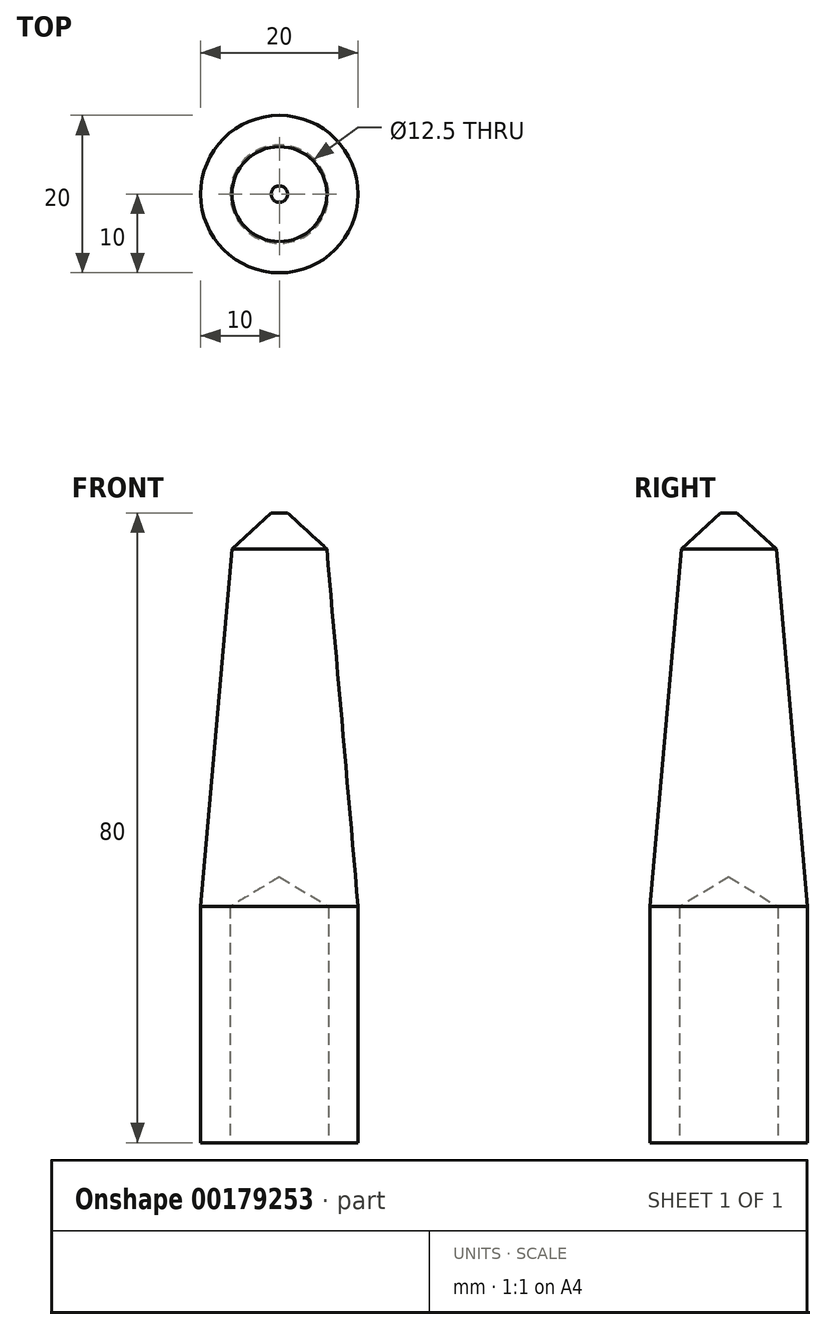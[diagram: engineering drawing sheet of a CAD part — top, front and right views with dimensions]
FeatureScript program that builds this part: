
annotation { "Feature Type Name" : "Feature", "Feature Type Description" : "" }
export const myFeature = defineFeature(function(context is Context, id is Id, definition is map)
    precondition{}
    {
        {
            var Q0;
            Q0=qCreatedBy(makeId("Top.planeOp"),FACE);
            var sketch = newSketch(context, id + "F0", { "sketchPlane" : qUnion([Q0])});
            skPoint(sketch, "E0", {"position": v(0, 0) * mm});
            skCircle(sketch, "E1", {"center": v(0, 0) * mm, "radius": 10 * mm});
            skSolve(sketch);
        }
        {
            var Q0;
            Q0=makeQuery(id+"F0.imprint","IMPRINT",FACE,{"disambiguationData":[TD([[makeQuery(id+"F0.imprint","IMPRINT",EDGE,{"derivedFrom":sQuery(id+"F0.wireOp",EDGE,"E1")}),1.0]])]});
            extrude(context, id + "F1", {"entities" : qUnion([Q0]), "depth" : 80 * mm});
        }
        {
            var Q0;
            Q0=makeQuery(id+"F1.opExtrude","CAP_EDGE",EDGE,{"disambiguationData":[OSD([sQuery(id+"F0.wireOp",EDGE,"E1")])],"isStart":false});
            chamfer(context, id + "F2", {"entities" : qUnion([Q0]), "chamferType" : ChamferType.OFFSET_ANGLE, "width" : 50 * mm, "oppositeDirection" : true, "angle" : 5 * degree, "tangentPropagation" : true});
        }
        {
            var Q0;
            {var subQ0=sQuery(id+"F0.wireOp",EDGE,"E1");Q0=makeQuery(id+"F2.opChamfer","BLEND_EDGE",EDGE,{"blendedFrom":[makeQuery(id+"F1.opExtrude","CAP_EDGE",EDGE,{"disambiguationData":[OSD([subQ0])],"isStart":false}),makeQuery(id+"F1.opExtrude","CAP_FACE",FACE,{"disambiguationData":[OSD([subQ0])],"isStart":false})],"blendedInto":[makeQuery(id+"F1.opExtrude","CAP_FACE",FACE,{"disambiguationData":[OSD([subQ0])],"isStart":false})]});}
            chamfer(context, id + "F3", {"entities" : qUnion([Q0]), "width" : 5 * mm, "tangentPropagation" : true});
        }
        {
            var Q0;
            Q0=qCreatedBy(makeId("Top.planeOp"),FACE);
            var sketch = newSketch(context, id + "F4", { "sketchPlane" : qUnion([Q0])});
            skPoint(sketch, "E2", {"position": v(0, 0) * mm});
            skSolve(sketch);
        }
        {
            var Q0;
            Q0=sQuery(id+"F4.wireOp",VERTEX,"E2");
            var Q1;
            Q1=makeQuery(id+"F1.opExtrude","SWEPT_BODY",BODY,{"disambiguationData":[OSD([sQuery(id+"F0.wireOp",EDGE,"E1")])]});
            hole(context, id + "F5", {"style" : HoleStyle.SIMPLE, "endStyle" : HoleEndStyle.BLIND, "oppositeDirection" : true, "holeDiameter" : 12.5 * mm, "holeDepth" : 30 * mm, "locations" : qUnion([Q0]), "scope" : qUnion([Q1])});
        }
    });
